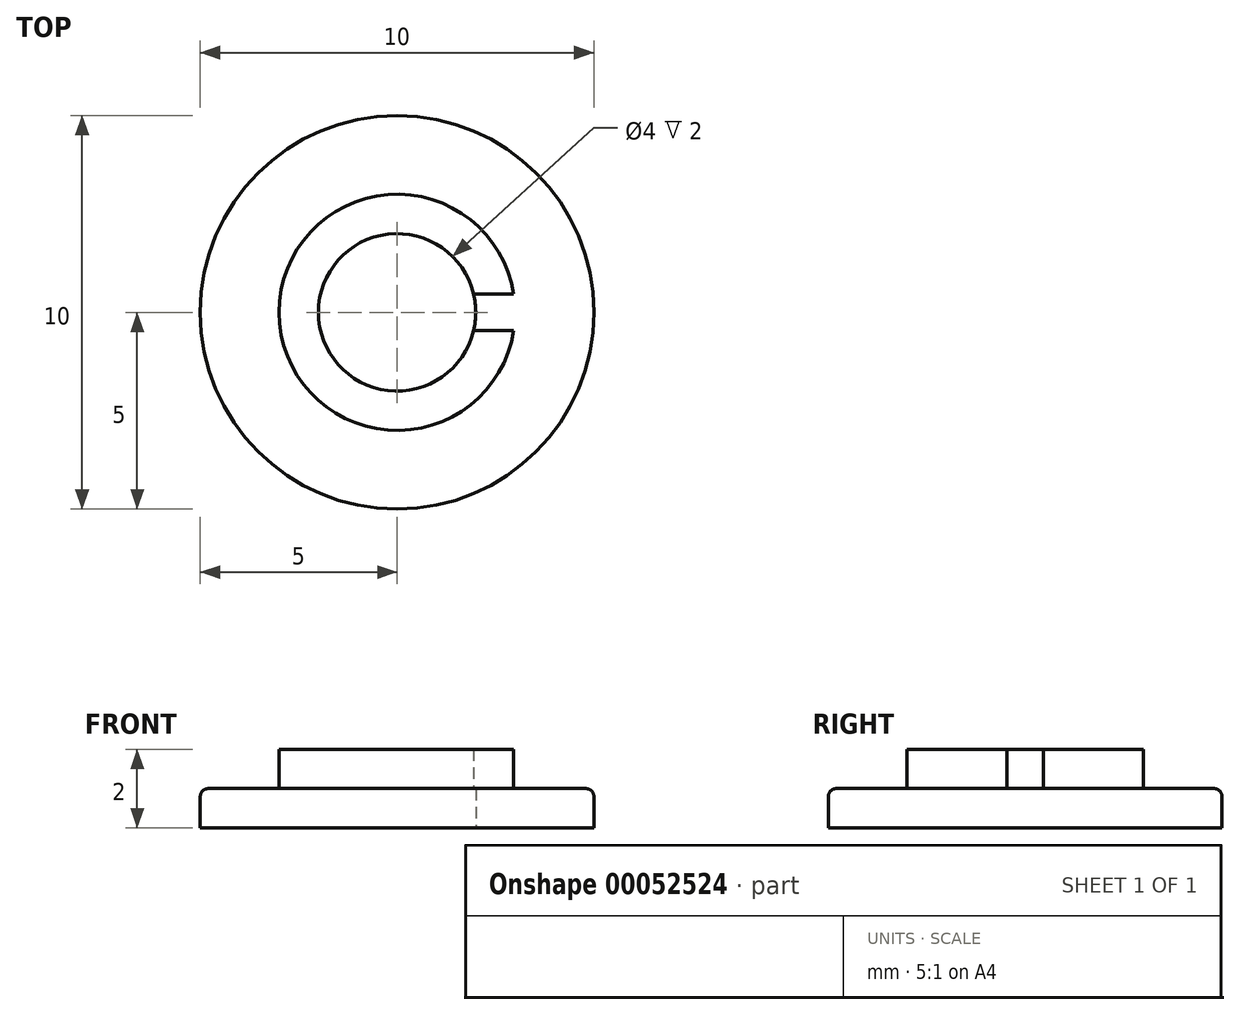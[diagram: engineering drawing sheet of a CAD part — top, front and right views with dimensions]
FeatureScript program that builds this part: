
annotation { "Feature Type Name" : "Feature", "Feature Type Description" : "" }
export const myFeature = defineFeature(function(context is Context, id is Id, definition is map)
    precondition{}
    {
        {
            var Q0;
            Q0=qCreatedBy(makeId("Top.planeOp"),FACE);
            var sketch = newSketch(context, id + "F0", { "sketchPlane" : qUnion([Q0])});
            skCircle(sketch, "E0", {"center": v(0, 0) * mm, "radius": 5 * mm});
            skCircle(sketch, "E1", {"center": v(0, 0) * mm, "radius": 2 * mm});
            skSolve(sketch);
        }
        {
            var Q0;
            Q0 = qSketchRegion(id + "F0", true);
            extrude(context, id + "F1", {"entities" : qUnion([Q0]), "depth" : 1 * mm});
        }
        {
            var Q0;
            Q0=makeQuery(id+"F1.opExtrude","CAP_FACE",FACE,{"disambiguationData":[OSD([sQuery(id+"F0.wireOp",EDGE,"E0")])],"isStart":false});
            var sketch = newSketch(context, id + "F2", { "sketchPlane" : qUnion([Q0])});
            skCircle(sketch, "E2", {"center": v(0, 0) * mm, "radius": 3 * mm});
            skCircle(sketch, "E3", {"center": v(0, 0) * mm, "radius": 2 * mm});
            skSolve(sketch);
        }
        {
            var Q0;
            Q0 = qSketchRegion(id + "F2", true);
            extrude(context, id + "F3", {"entities" : qUnion([Q0]), "operationType" : NewBodyOperationType.ADD, "depth" : 1 * mm});
        }
        {
            var Q0;
            Q0=makeQuery(id+"F3.opExtrude","CAP_FACE",FACE,{"disambiguationData":[OSD([sQuery(id+"F2.wireOp",EDGE,"E2"),sQuery(id+"F2.wireOp",EDGE,"E3")])],"isStart":false});
            var sketch = newSketch(context, id + "F4", { "sketchPlane" : qUnion([Q0])});
            skLineSegment(sketch, "E4", {"start": v(0, 0) * mm, "end": v(4.17, 0) * mm, "construction": true});
            skLineSegment(sketch, "E5.rect.bottom", {"start": v(3.67, -0.47) * mm, "end": v(1.22, -0.47) * mm});
            skLineSegment(sketch, "E5.rect.top", {"start": v(3.67, 0.47) * mm, "end": v(1.22, 0.47) * mm});
            skLineSegment(sketch, "E5.rect.left", {"start": v(3.67, -0.47) * mm, "end": v(3.67, 0.47) * mm});
            skLineSegment(sketch, "E5.rect.right", {"start": v(1.22, -0.47) * mm, "end": v(1.22, 0.47) * mm});
            skPoint(sketch, "E5.rect.middle", {"position": v(2.45, 0) * mm});
            skSolve(sketch);
        }
        {
            var Q0;
            Q0 = qSketchRegion(id + "F4", true);
            extrude(context, id + "F5", {"entities" : qUnion([Q0]), "operationType" : NewBodyOperationType.REMOVE, "oppositeDirection" : true, "depth" : 1 * mm});
        }
        {
            var Q0;
            Q0=makeQuery(id+"F1.opExtrude","CAP_EDGE",EDGE,{"disambiguationData":[OSD([sQuery(id+"F0.wireOp",EDGE,"E0")])],"isStart":false});
            fillet(context, id + "F6", {"entities" : qUnion([Q0]), "radius" : 0.2 * mm, "tangentPropagation" : true, "allowEdgeOverflow" : false});
        }
    });
